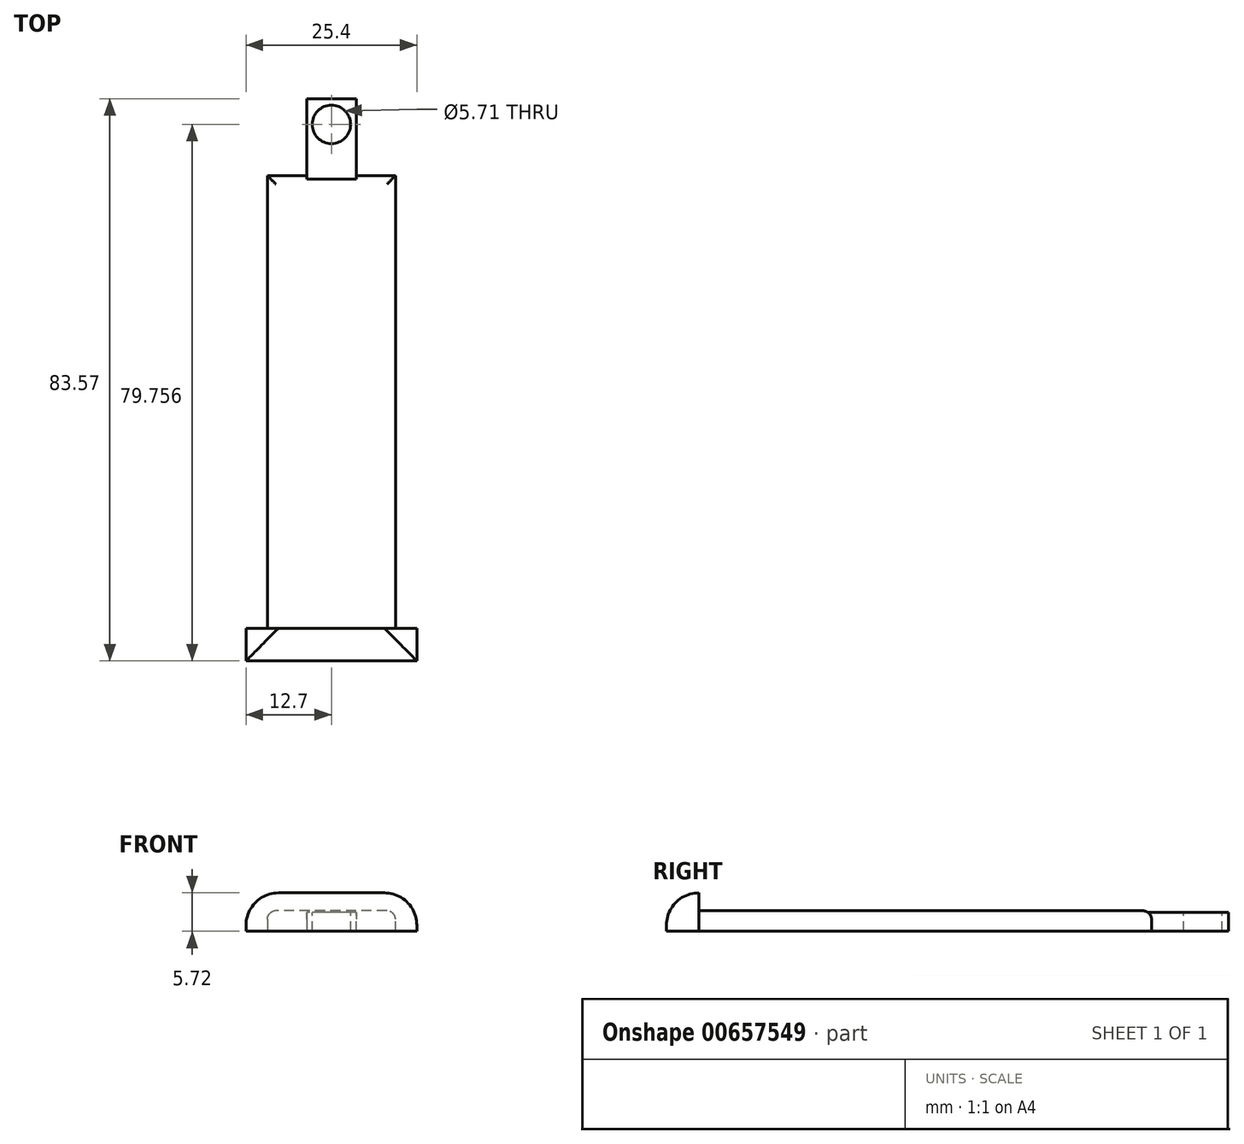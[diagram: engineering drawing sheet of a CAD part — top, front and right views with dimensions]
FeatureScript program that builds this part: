
annotation { "Feature Type Name" : "Feature", "Feature Type Description" : "" }
export const myFeature = defineFeature(function(context is Context, id is Id, definition is map)
    precondition{}
    {
        {
            var Q0;
            Q0=qCreatedBy(makeId("Front.planeOp"),FACE);
            var sketch = newSketch(context, id + "F0", { "sketchPlane" : qUnion([Q0])});
            skLineSegment(sketch, "E0.bottom", {"start": v(0, 0) * mm, "end": v(9.53, 0) * mm});
            skLineSegment(sketch, "E0.top", {"start": v(0, 5.72) * mm, "end": v(9.53, 5.72) * mm});
            skLineSegment(sketch, "E0.left", {"start": v(0, 0) * mm, "end": v(0, 5.72) * mm});
            skLineSegment(sketch, "E0.right", {"start": v(9.53, 0) * mm, "end": v(9.53, 5.71) * mm});
            skLineSegment(sketch, "E1.bottom", {"start": v(0, 0) * mm, "end": v(-9.53, 0) * mm});
            skLineSegment(sketch, "E1.top", {"start": v(0, 5.72) * mm, "end": v(-9.53, 5.72) * mm});
            skLineSegment(sketch, "E1.right", {"start": v(-9.53, 0) * mm, "end": v(-9.53, 5.71) * mm});
            skSolve(sketch);
        }
        {
            var Q0;
            Q0 = qSketchRegion(id + "F0", true);
            extrude(context, id + "F1", {"entities" : qUnion([Q0]), "oppositeDirection" : true, "depth" : 4.83 * mm, "offsetDistance" : 25.4 * mm});
        }
        {
            var Q0;
            Q0=makeQuery(id+"F1.opExtrude","CAP_FACE",FACE,{"disambiguationData":[OSD([sQuery(id+"F0.wireOp",EDGE,"E0.bottom"),sQuery(id+"F0.wireOp",EDGE,"E0.top"),sQuery(id+"F0.wireOp",EDGE,"E0.right"),sQuery(id+"F0.wireOp",EDGE,"E1.bottom"),sQuery(id+"F0.wireOp",EDGE,"E1.top"),sQuery(id+"F0.wireOp",EDGE,"E1.right")])],"isStart":false});
            var sketch = newSketch(context, id + "F2", { "sketchPlane" : qUnion([Q0])});
            skLineSegment(sketch, "E2.bottom", {"start": v(-9.53, 0) * mm, "end": v(9.53, 0) * mm});
            skLineSegment(sketch, "E2.top", {"start": v(-9.53, 3.05) * mm, "end": v(9.53, 3.05) * mm});
            skLineSegment(sketch, "E2.left", {"start": v(-9.53, 0) * mm, "end": v(-9.53, 3.05) * mm});
            skLineSegment(sketch, "E2.right", {"start": v(9.53, 0) * mm, "end": v(9.53, 3.05) * mm});
            skSolve(sketch);
        }
        {
            var Q0;
            Q0 = qSketchRegion(id + "F2", true);
            extrude(context, id + "F3", {"entities" : qUnion([Q0]), "operationType" : NewBodyOperationType.ADD, "depth" : 67.3 * mm, "offsetDistance" : 25.4 * mm});
        }
        {
            var Q0;
            Q0=makeQuery(id+"F3.opExtrude","SWEPT_EDGE",EDGE,{"disambiguationData":[OSD([sQuery(id+"F0.wireOp",EDGE,"E0.right"),sQuery(id+"F2.wireOp",EDGE,"E2.top"),sQuery(id+"F2.wireOp",EDGE,"E2.left")])]});
            var Q1;
            Q1=makeQuery(id+"F3.opExtrude","SWEPT_EDGE",EDGE,{"disambiguationData":[OSD([sQuery(id+"F0.wireOp",EDGE,"E1.right"),sQuery(id+"F2.wireOp",EDGE,"E2.top"),sQuery(id+"F2.wireOp",EDGE,"E2.right")])]});
            var Q2;
            Q2=makeQuery(id+"F3.opExtrude","CAP_EDGE",EDGE,{"disambiguationData":[OSD([sQuery(id+"F2.wireOp",EDGE,"E2.top")])],"isStart":false});
            fillet(context, id + "F4", {"entities" : qUnion([Q0, Q1, Q2]), "radius" : 1.27 * mm, "tangentPropagation" : true, "allowEdgeOverflow" : false});
        }
        {
            var Q0;
            Q0=makeQuery(id+"F3.opExtrude","CAP_FACE",FACE,{"disambiguationData":[OSD([sQuery(id+"F2.wireOp",EDGE,"E2.bottom"),sQuery(id+"F2.wireOp",EDGE,"E2.top"),sQuery(id+"F2.wireOp",EDGE,"E2.left"),sQuery(id+"F2.wireOp",EDGE,"E2.right")])],"isStart":false});
            var sketch = newSketch(context, id + "F5", { "sketchPlane" : qUnion([Q0])});
            skSolve(sketch);
        }
        {
            var Q0;
            {var subQ0=sQuery(id+"F2.wireOp",EDGE,"E2.bottom");Q0=makeQuery(id+"F5.imprint","IMPRINT",FACE,{"disambiguationData":[TD([[makeQuery(id+"F5.imprint","IMPRINT",EDGE,{"derivedFrom":makeQuery(id+"F3.opExtrude","CAP_EDGE",EDGE,{"disambiguationData":[OSD([subQ0])],"isStart":false})}),-1.0]])]});}
            var sketch = newSketch(context, id + "F6", { "sketchPlane" : qUnion([Q0])});
            skLineSegment(sketch, "E3", {"start": v(0, 0) * mm, "end": v(-3.68, 0) * mm});
            skLineSegment(sketch, "E4", {"start": v(-3.68, 0) * mm, "end": v(-3.68, 2.8) * mm});
            skLineSegment(sketch, "E5", {"start": v(-3.68, 2.8) * mm, "end": v(3.68, 2.8) * mm});
            skLineSegment(sketch, "E6", {"start": v(3.68, 2.8) * mm, "end": v(3.68, 0) * mm});
            skLineSegment(sketch, "E7", {"start": v(3.68, 0) * mm, "end": v(0, 0) * mm});
            skSolve(sketch);
        }
        {
            var Q0;
            Q0 = qSketchRegion(id + "F6", true);
            extrude(context, id + "F7", {"entities" : qUnion([Q0]), "operationType" : NewBodyOperationType.ADD, "depth" : 11.43 * mm, "offsetDistance" : 25.4 * mm});
        }
        {
            var Q0;
            Q0=makeQuery(id+"F7.opExtrude","SWEPT_FACE",FACE,{"disambiguationData":[OSD([sQuery(id+"F6.wireOp",EDGE,"E5")])]});
            var sketch = newSketch(context, id + "F8", { "sketchPlane" : qUnion([Q0])});
            skLineSegment(sketch, "E8", {"start": v(-3.68, 83.57) * mm, "end": v(-3.68, 75.95) * mm});
            skCircle(sketch, "E9", {"center": v(0, 79.76) * mm, "radius": 2.86 * mm});
            skPoint(sketch, "E9.centerSnap0", {"position": v(-3.68, 79.76) * mm});
            skPoint(sketch, "E9.centerSnap1", {"position": v(0, 83.57) * mm});
            skSolve(sketch);
        }
        {
            var Q0;
            Q0 = qSketchRegion(id + "F8", true);
            extrude(context, id + "F9", {"entities" : qUnion([Q0]), "operationType" : NewBodyOperationType.REMOVE, "oppositeDirection" : true, "depth" : 25.4 * mm, "offsetDistance" : 25.4 * mm});
        }
        {
            var Q0;
            Q0=makeQuery(id+"F7.opExtrude","CAP_FACE",FACE,{"disambiguationData":[OSD([sQuery(id+"F6.wireOp",EDGE,"E3"),sQuery(id+"F6.wireOp",EDGE,"E4"),sQuery(id+"F6.wireOp",EDGE,"E5"),sQuery(id+"F6.wireOp",EDGE,"E6"),sQuery(id+"F6.wireOp",EDGE,"E7")])],"isStart":true});
            extrude(context, id + "F10", {"entities" : qUnion([Q0]), "operationType" : NewBodyOperationType.ADD, "depth" : 25.4 * mm, "offsetDistance" : 25.4 * mm});
        }
        {
            var Q0;
            Q0=makeQuery(id+"F3.boolean.opBoolean","MERGE",FACE,{"derivedFrom":[makeQuery(id+"F1.opExtrude","SWEPT_FACE",FACE,{"disambiguationData":[OSD([sQuery(id+"F0.wireOp",EDGE,"E0.right")])]}),makeQuery(id+"F3.opExtrude","SWEPT_FACE",FACE,{"disambiguationData":[OSD([sQuery(id+"F2.wireOp",EDGE,"E2.left")])]})]});
            var sketch = newSketch(context, id + "F11", { "sketchPlane" : qUnion([Q0])});
            skLineSegment(sketch, "E10", {"start": v(4.83, 1.78) * mm, "end": v(4.83, 0) * mm});
            skSolve(sketch);
        }
        {
            var Q0;
            {var subQ2=sQuery(id+"F11.wireOp",EDGE,"E10");Q0=makeQuery(id+"F11.imprint","IMPRINT",FACE,{"disambiguationData":[TD([[makeQuery(id+"F11.imprint","IMPRINT",EDGE,{"derivedFrom":subQ2}),-1.0]])]});}
            extrude(context, id + "F12", {"entities" : qUnion([Q0]), "operationType" : NewBodyOperationType.ADD, "oppositeDirection" : true, "depth" : 22.22 * mm, "offsetDistance" : 25.4 * mm});
        }
        {
            var Q0;
            {var subQ2=sQuery(id+"F11.wireOp",EDGE,"E10");Q0=makeQuery(id+"F11.imprint","IMPRINT",FACE,{"disambiguationData":[TD([[makeQuery(id+"F11.imprint","IMPRINT",EDGE,{"derivedFrom":subQ2}),-1.0]])]});}
            extrude(context, id + "F13", {"entities" : qUnion([Q0]), "operationType" : NewBodyOperationType.ADD, "depth" : 3.17 * mm, "offsetDistance" : 25.4 * mm});
        }
        {
            var Q0;
            Q0=makeQuery(id+"F13.opExtrude","CAP_EDGE",EDGE,{"disambiguationData":[OSD([sQuery(id+"F0.wireOp",EDGE,"E0.top"),sQuery(id+"F0.wireOp",EDGE,"E0.right")])],"isStart":false});
            var Q1;
            Q1=makeQuery(id+"F12.opExtrude","CAP_EDGE",EDGE,{"disambiguationData":[OSD([sQuery(id+"F0.wireOp",EDGE,"E0.top"),sQuery(id+"F0.wireOp",EDGE,"E0.right")])],"isStart":false});
            var Q2;
            {var subQ0=sQuery(id+"F0.wireOp",EDGE,"E0.right");var subQ1=sQuery(id+"F0.wireOp",EDGE,"E0.top");var subQ2=makeQuery(id+"F11.imprint","INTERSECT",VERTEX,{"derivedFrom":[makeQuery(id+"F1.opExtrude","SWEPT_EDGE",EDGE,{"disambiguationData":[OSD([subQ1,subQ0])]}),makeQuery(id+"F1.opExtrude","CAP_EDGE",EDGE,{"disambiguationData":[OSD([subQ0])],"isStart":true})]});Q2=makeQuery(id+"F13.boolean.opBoolean","MERGE",EDGE,{"derivedFrom":[makeQuery(id+"F12.boolean.opBoolean","MERGE",EDGE,{"derivedFrom":[makeQuery(id+"F1.opExtrude","CAP_EDGE",EDGE,{"disambiguationData":[OSD([subQ1,sQuery(id+"F0.wireOp",EDGE,"E1.top")])],"isStart":true}),makeQuery(id+"F12.opExtrude","SWEPT_EDGE",EDGE,{"disambiguationData":[OSD([subQ1,subQ0]),TDD([subQ2])]})]}),makeQuery(id+"F13.opExtrude","SWEPT_EDGE",EDGE,{"disambiguationData":[OSD([subQ1,subQ0]),TDD([subQ2])]})]});}
            fillet(context, id + "F14", {"entities" : qUnion([Q0, Q1, Q2]), "radius" : 4.83 * mm, "tangentPropagation" : true, "allowEdgeOverflow" : false});
        }
    });
